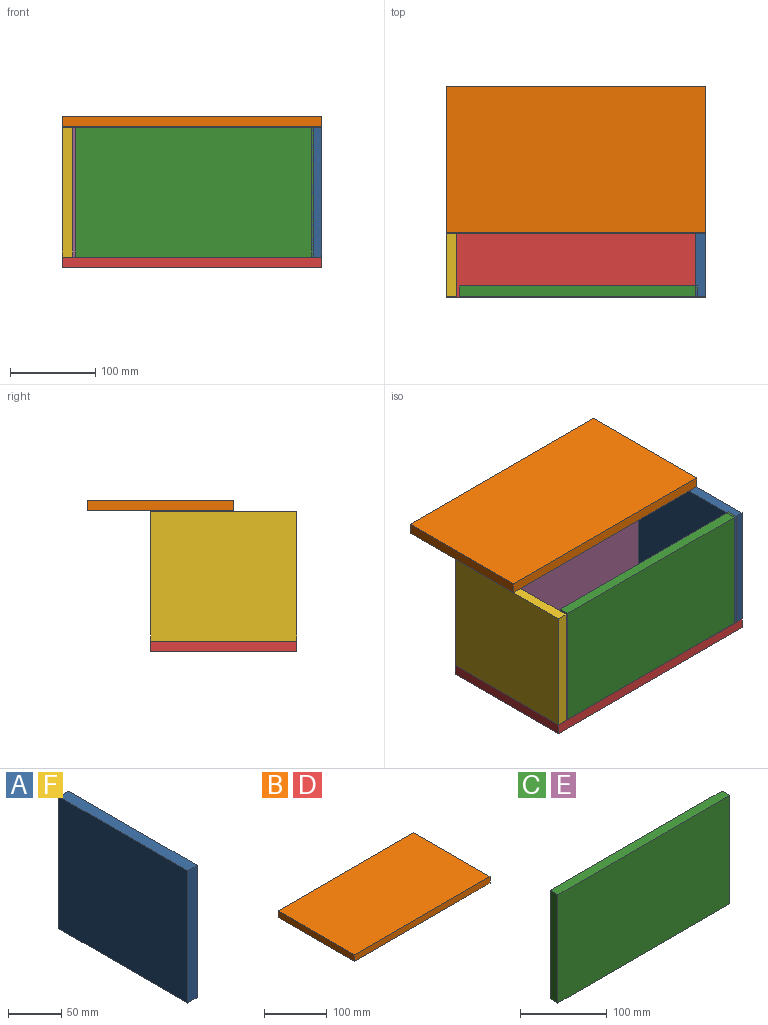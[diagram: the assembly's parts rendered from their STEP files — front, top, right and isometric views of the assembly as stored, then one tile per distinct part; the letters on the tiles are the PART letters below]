
ASSEMBLY  parts=6 mates=9
PART A: 6 faces, bbox 12.7x171.5x152.4 mm
  f0: plane 152.4x12.7mm, normal (0,-1,0), area 1935.5mm2, adj f1,f3,f4,f5
  f1: plane 171.45x152.4mm, normal (1,0,0), area 26129mm2, adj f0,f2,f4,f5
  f2: plane 152.4x12.7mm, normal (0,1,0), area 1935.5mm2, adj f1,f3,f4,f5
  f3: plane 171.45x152.4mm, normal (-1,0,0), area 26129mm2, adj f0,f2,f4,f5
  f4: plane 171.45x12.7mm, normal (0,0,1), area 2177.4mm2, adj f0,f1,f2,f3
  f5: plane 171.45x12.7mm, normal (0,0,-1), area 2177.4mm2, adj f0,f1,f2,f3
PART B: 6 faces, bbox 304.8x171.5x12.7 mm
  f0: plane 304.8x12.7mm, normal (0,-1,0), area 3871mm2, adj f1,f3,f4,f5
  f1: plane 171.45x12.7mm, normal (1,0,0), area 2177.4mm2, adj f0,f2,f4,f5
  f2: plane 304.8x12.7mm, normal (0,1,0), area 3871mm2, adj f1,f3,f4,f5
  f3: plane 171.45x12.7mm, normal (-1,0,0), area 2177.4mm2, adj f0,f2,f4,f5
  f4: plane 304.8x171.45mm, normal (0,0,1), area 52258mm2, adj f0,f1,f2,f3
  f5: plane 304.8x171.45mm, normal (0,0,-1), area 52258mm2, adj f0,f1,f2,f3
PART C: 6 faces, bbox 279.4x12.7x152.4 mm
  f0: plane 279.4x152.4mm, normal (0,-1,0), area 42580.6mm2, adj f1,f3,f4,f5
  f1: plane 152.4x12.7mm, normal (1,0,0), area 1935.5mm2, adj f0,f2,f4,f5
  f2: plane 279.4x152.4mm, normal (0,1,0), area 42580.6mm2, adj f1,f3,f4,f5
  f3: plane 152.4x12.7mm, normal (-1,0,0), area 1935.5mm2, adj f0,f2,f4,f5
  f4: plane 279.4x12.7mm, normal (0,0,1), area 3548.4mm2, adj f0,f1,f2,f3
  f5: plane 279.4x12.7mm, normal (0,0,-1), area 3548.4mm2, adj f0,f1,f2,f3
PART D: same geometry as B
PART E: same geometry as C
PART F: same geometry as A
PLACE A t=(146.05,0,12.7)mm
PLACE B t=(0,74.9,165.39)mm
PLACE C t=(2.83,-79.38,12.7)mm
PLACE D at identity fixed
PLACE E t=(0,79.38,12.7)mm
PLACE F rot(axis=(0,1,0),180deg) t=(-146.05,0,165.1)mm
MATE planar E.f2 <-> D.f2  axis (0,1,0) through (0,85.73,88.9)mm
MATE planar C.f0 <-> D.f0  axis (0,-1,0) through (2.83,-85.72,88.9)mm
MATE planar E.f5 <-> D.f4  axis (0,0,-1) through (0,79.38,12.7)mm
MATE planar F.f1 <-> D.f3  axis (-1,0,0) through (-152.4,0,88.9)mm
MATE planar D.f4 <-> F.f4  axis (0,0,1) through (0,0,12.7)mm
MATE planar D.f4 <-> A.f5  axis (0,0,1) through (0,0,12.7)mm
MATE planar B.f3 <-> F.f1  axis (-1,0,0) through (-152.4,74.9,171.74)mm
MATE planar D.f4 <-> C.f5  axis (0,0,1) through (0,0,12.7)mm
MATE planar A.f1 <-> D.f1  axis (1,0,0) through (152.4,0,88.9)mm
